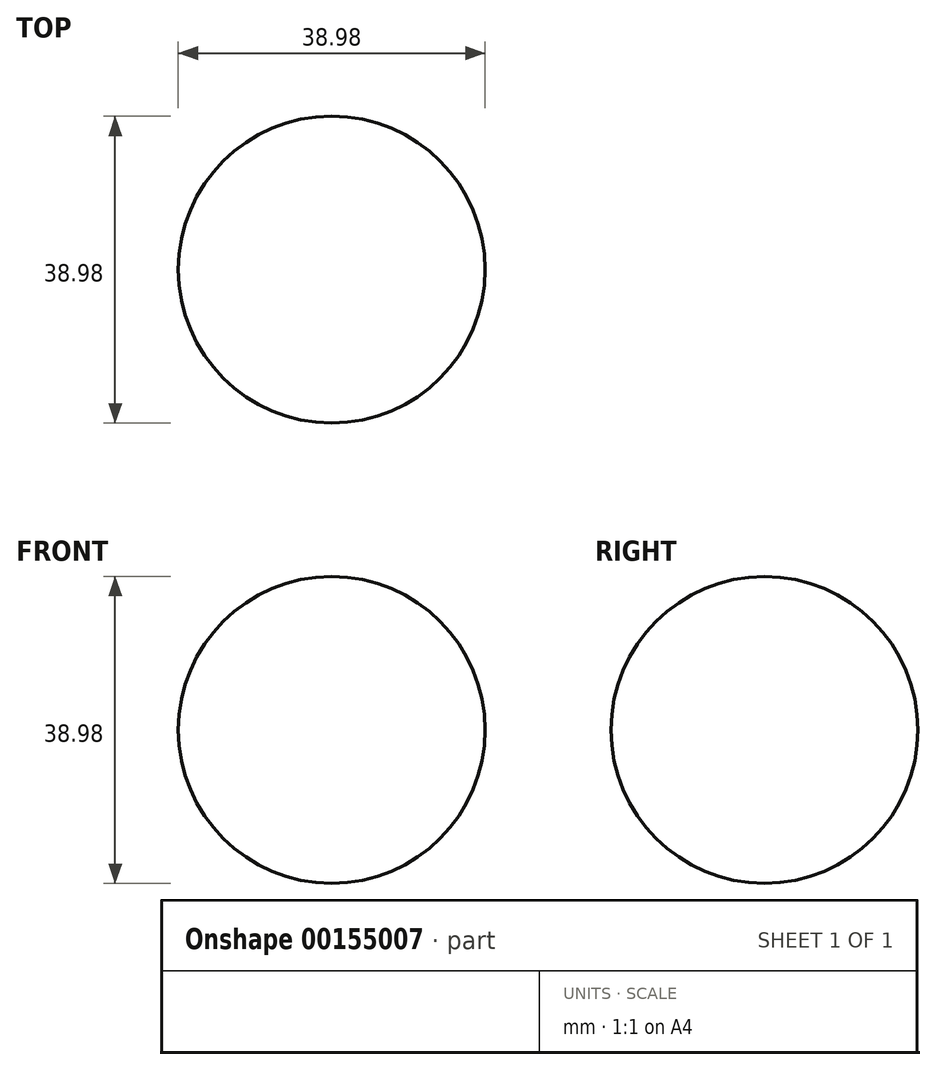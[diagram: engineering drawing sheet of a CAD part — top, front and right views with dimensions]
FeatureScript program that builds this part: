
annotation { "Feature Type Name" : "Feature", "Feature Type Description" : "" }
export const myFeature = defineFeature(function(context is Context, id is Id, definition is map)
    precondition{}
    {
        {
            var Q0;
            Q0=qCreatedBy(makeId("Top.planeOp"),FACE);
            var sketch = newSketch(context, id + "F0", { "sketchPlane" : qUnion([Q0])});
            skArc(sketch, "E0", {"start": v(0, -19.49) * mm, "mid": v(19.49, 0) * mm, "end": v(0, 19.49) * mm});
            skLineSegment(sketch, "E1", {"start": v(0, -19.49) * mm, "end": v(0, 19.49) * mm});
            skLineSegment(sketch, "E2", {"start": v(0, 46.46) * mm, "end": v(0, -42.6) * mm, "construction": true});
            skSolve(sketch);
        }
        {
            var Q0;
            Q0 = qSketchRegion(id + "F0", true);
            var Q1;
            Q1=sQuery(id+"F0.wireOp",EDGE,"E2");
            revolve(context, id + "F1", {"surfaceOperationType" : NewSurfaceOperationType.NEW, "entities" : qUnion([Q0]), "axis" : qUnion([Q1]), "revolveType" : RevolveType.FULL});
        }
    });
